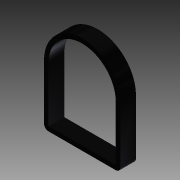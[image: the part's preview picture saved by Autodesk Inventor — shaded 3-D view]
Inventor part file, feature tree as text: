
AUTODESK INVENTOR PART (.ipt)
format: ipt  version: 2013 (Build 170138000, 138)  size: 89,600 bytes
history: native  units: in
note: dims shown in document units (in); Inventor stores cm internally (conversion verified against a paired STEP export)
features: reference x3, extrude x1, fillet x1, sketch x1
ambient origin geometry x8: Origin, YZ Plane, XZ Plane, XY Plane, X Axis, Y Axis, Z Axis, Center Point
bodies: Solid1 (feature_tree)
feature tree (6):
  extrude  "Extrusion1"  Depth=0.1378in TaperAngle=0.0deg
  fillet  "Fillet1"  Radius=0.0394in
  sketch  "Sketch1"  dims[d0=0.0394in d1=0.1378in d2=0.0in d3=0.0394in]
  reference  "Reference1"
  reference  "Reference2"
  reference  "Reference3"
